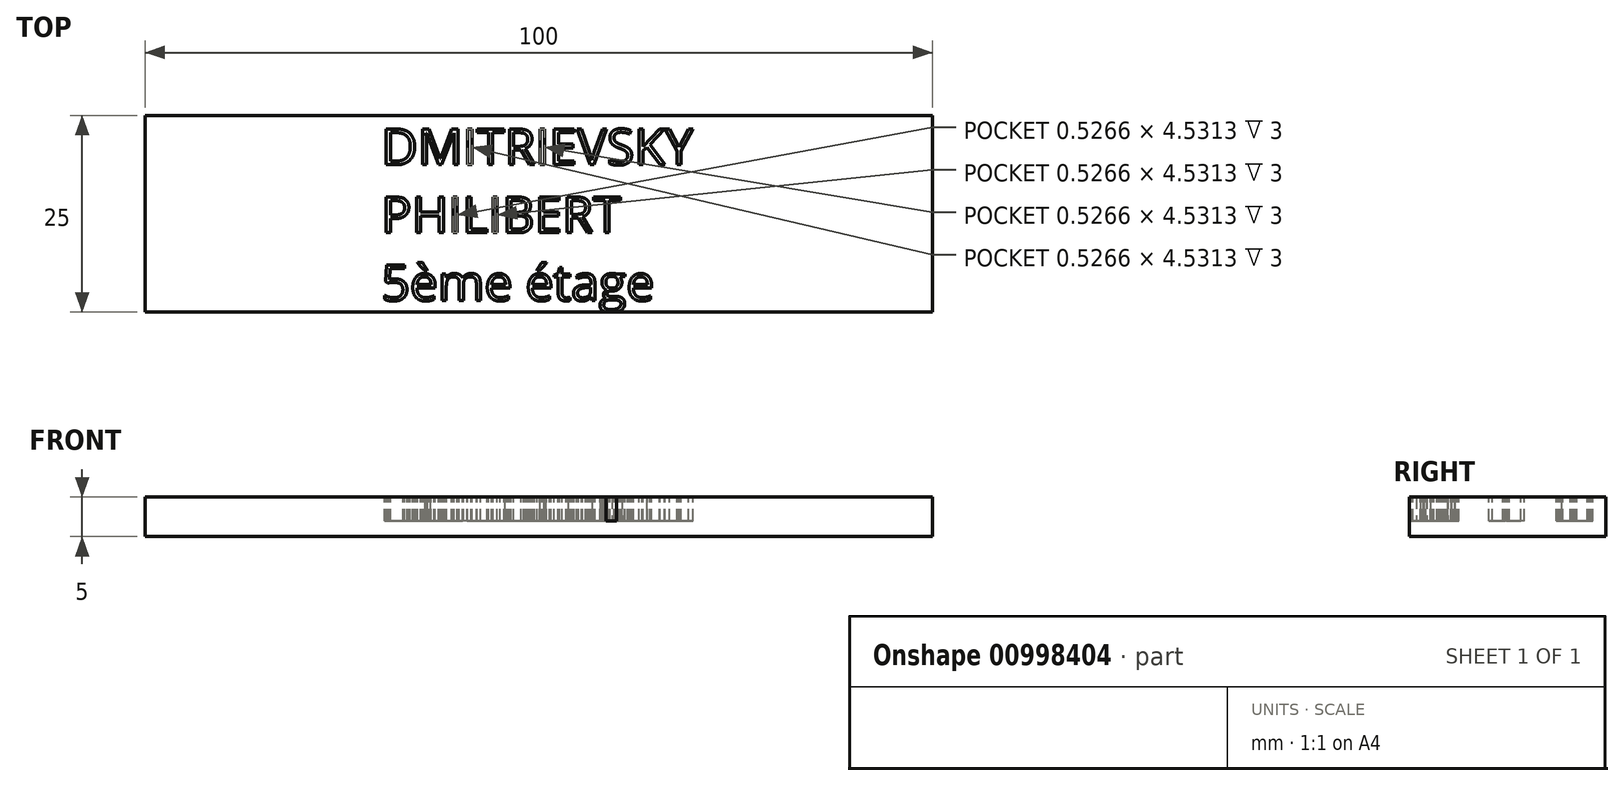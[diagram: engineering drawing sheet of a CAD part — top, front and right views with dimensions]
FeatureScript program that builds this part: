
annotation { "Feature Type Name" : "Feature", "Feature Type Description" : "" }
export const myFeature = defineFeature(function(context is Context, id is Id, definition is map)
    precondition{}
    {
        {
            var Q0;
            Q0=qCreatedBy(makeId("Top.planeOp"),FACE);
            var sketch = newSketch(context, id + "F0", { "sketchPlane" : qUnion([Q0])});
            skLineSegment(sketch, "E0.bottom", {"start": v(-113.85, -14.33) * mm, "end": v(-13.85, -14.33) * mm});
            skLineSegment(sketch, "E0.top", {"start": v(-113.85, -39.33) * mm, "end": v(-13.85, -39.33) * mm});
            skLineSegment(sketch, "E0.left", {"start": v(-113.85, -14.33) * mm, "end": v(-113.85, -39.33) * mm});
            skLineSegment(sketch, "E0.right", {"start": v(-13.85, -14.33) * mm, "end": v(-13.85, -39.33) * mm});
            skSolve(sketch);
        }
        {
            var Q0;
            Q0=makeQuery(id+"F0.imprint","IMPRINT",FACE,{"disambiguationData":[TD([[makeQuery(id+"F0.imprint","IMPRINT",EDGE,{"derivedFrom":sQuery(id+"F0.wireOp",EDGE,"E0.bottom")}),-1.0]])]});
            extrude(context, id + "F1", {"entities" : qUnion([Q0]), "depth" : 5 * mm, "offsetDistance" : 25 * mm});
        }
        {
            var Q0;
            Q0=makeQuery(id+"F1.opExtrude","CAP_FACE",FACE,{"disambiguationData":[OSD([sQuery(id+"F0.wireOp",EDGE,"E0.bottom"),sQuery(id+"F0.wireOp",EDGE,"E0.top"),sQuery(id+"F0.wireOp",EDGE,"E0.left"),sQuery(id+"F0.wireOp",EDGE,"E0.right")])],"isStart":false});
            var sketch = newSketch(context, id + "F2", { "sketchPlane" : qUnion([Q0])});
            skText(sketch, "E1", { "text": "DMITRIEVSKY\nPHILIBERT\n5ème étage", "fontName": "OpenSans-Regular.ttf"});
            const initialGuessF2  = {"E1": [-0.08385, -0.0206, 1, 0, 0.00457]};
            skSetInitialGuess(sketch, initialGuessF2);
            skSolve(sketch);
        }
        {
            var Q0;
            Q0 = qSketchRegion(id + "F2", true);
            extrude(context, id + "F3", {"entities" : qUnion([Q0]), "operationType" : NewBodyOperationType.REMOVE, "oppositeDirection" : true, "depth" : 3 * mm, "offsetDistance" : 25 * mm});
        }
    });
